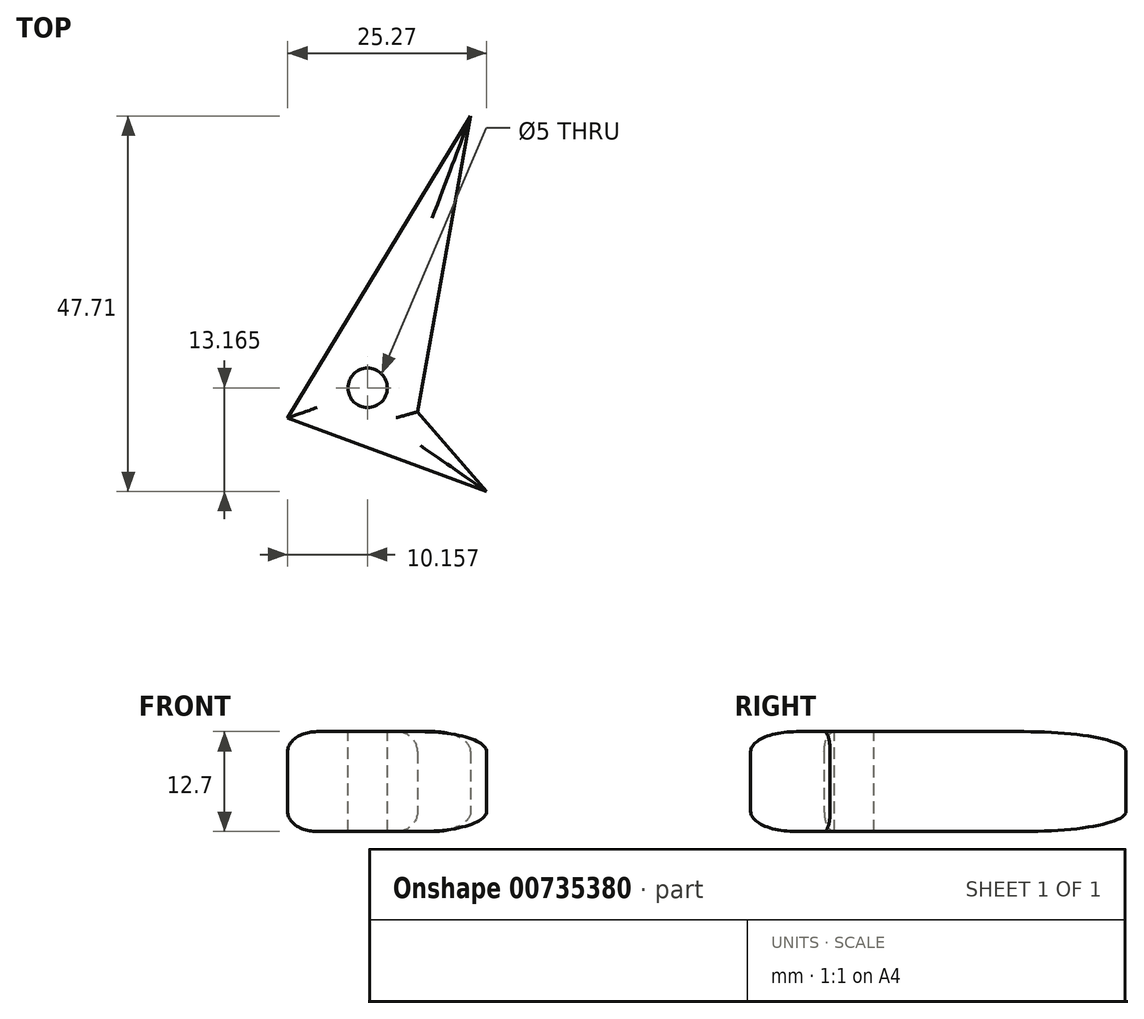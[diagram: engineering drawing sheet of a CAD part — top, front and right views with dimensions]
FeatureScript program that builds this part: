
annotation { "Feature Type Name" : "Feature", "Feature Type Description" : "" }
export const myFeature = defineFeature(function(context is Context, id is Id, definition is map)
    precondition{}
    {
        {
            var Q0;
            Q0=qCreatedBy(makeId("Top.planeOp"),FACE);
            var sketch = newSketch(context, id + "F0", { "sketchPlane" : qUnion([Q0])});
            skLineSegment(sketch, "E0", {"start": v(-25.27, 15.88) * mm, "end": v(-2.01, 54.23) * mm});
            skLineSegment(sketch, "E1", {"start": v(-2.01, 54.23) * mm, "end": v(-8.76, 16.64) * mm});
            skLineSegment(sketch, "E2", {"start": v(-8.76, 16.64) * mm, "end": v(-25.27, 15.88) * mm});
            skLineSegment(sketch, "E3", {"start": v(-25.27, 15.88) * mm, "end": v(0, 6.52) * mm});
            skLineSegment(sketch, "E4", {"start": v(-8.76, 16.64) * mm, "end": v(0, 6.52) * mm});
            skSolve(sketch);
        }
        {
            var Q0;
            Q0=makeQuery(id+"F0.imprint","IMPRINT",FACE,{"disambiguationData":[TD([[makeQuery(id+"F0.imprint","IMPRINT",EDGE,{"derivedFrom":sQuery(id+"F0.wireOp",EDGE,"E0")}),-1.0]])]});
            var Q1;
            Q1=makeQuery(id+"F0.imprint","IMPRINT",FACE,{"disambiguationData":[TD([[makeQuery(id+"F0.imprint","IMPRINT",EDGE,{"derivedFrom":sQuery(id+"F0.wireOp",EDGE,"E2")}),1.0]])]});
            extrude(context, id + "F1", {"entities" : qUnion([Q0, Q1]), "depth" : 12.7 * mm, "offsetDistance" : 25.4 * mm});
        }
        {
            var Q0;
            Q0=makeQuery(id+"F1.opExtrude","CAP_FACE",FACE,{"disambiguationData":[OSD([sQuery(id+"F0.wireOp",EDGE,"E0"),sQuery(id+"F0.wireOp",EDGE,"E1"),sQuery(id+"F0.wireOp",EDGE,"lH39WLJO-WQOK-cSMH-3CBh-9aL3xs9QHxXM"),sQuery(id+"F0.wireOp",EDGE,"HwrzEew4-jBMB-fb36-PGyb-4g7qYyCsIXHj")])],"isStart":false});
            fillet(context, id + "F2", {"entities" : qUnion([Q0]), "radius" : 2.54 * mm, "tangentPropagation" : true, "allowEdgeOverflow" : false});
        }
        {
            var Q0;
            Q0=makeQuery(id+"F1.opExtrude","CAP_FACE",FACE,{"disambiguationData":[OSD([sQuery(id+"F0.wireOp",EDGE,"E0"),sQuery(id+"F0.wireOp",EDGE,"E1"),sQuery(id+"F0.wireOp",EDGE,"lH39WLJO-WQOK-cSMH-3CBh-9aL3xs9QHxXM"),sQuery(id+"F0.wireOp",EDGE,"HwrzEew4-jBMB-fb36-PGyb-4g7qYyCsIXHj")])],"isStart":true});
            fillet(context, id + "F3", {"entities" : qUnion([Q0]), "radius" : 2.54 * mm, "tangentPropagation" : true, "allowEdgeOverflow" : false});
        }
        {
            var Q0;
            Q0=makeQuery(id+"F1.opExtrude","CAP_FACE",FACE,{"disambiguationData":[OSD([sQuery(id+"F0.wireOp",EDGE,"E0"),sQuery(id+"F0.wireOp",EDGE,"E1"),sQuery(id+"F0.wireOp",EDGE,"E3"),sQuery(id+"F0.wireOp",EDGE,"E4")])],"isStart":false});
            var sketch = newSketch(context, id + "F4", { "sketchPlane" : qUnion([Q0])});
            skCircle(sketch, "E5", {"center": v(-15.11, 19.69) * mm, "radius": 2.5 * mm});
            skSolve(sketch);
        }
        {
            var Q0;
            Q0=makeQuery(id+"F4.imprint","IMPRINT",FACE,{"disambiguationData":[TD([[makeQuery(id+"F4.imprint","IMPRINT",EDGE,{"derivedFrom":sQuery(id+"F4.wireOp",EDGE,"E5")}),1.0]])]});
            extrude(context, id + "F5", {"entities" : qUnion([Q0]), "operationType" : NewBodyOperationType.REMOVE, "oppositeDirection" : true, "depth" : 12.95 * mm, "offsetDistance" : 25.4 * mm});
        }
    });
